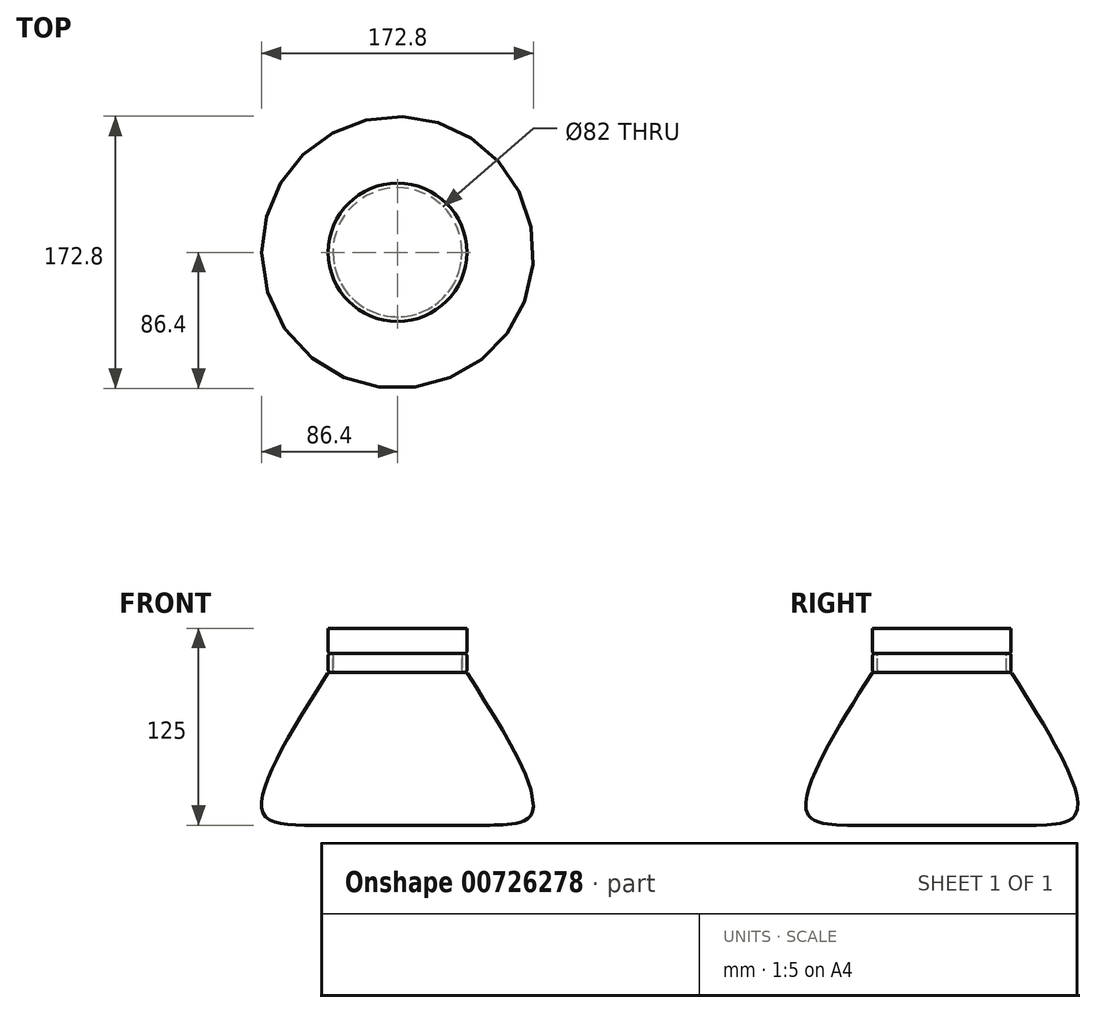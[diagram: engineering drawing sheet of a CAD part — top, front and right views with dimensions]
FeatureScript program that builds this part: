
annotation { "Feature Type Name" : "Feature", "Feature Type Description" : "" }
export const myFeature = defineFeature(function(context is Context, id is Id, definition is map)
    precondition{}
    {
        {
            var Q0;
            Q0=qCreatedBy(makeId("Front.planeOp"),FACE);
            var sketch = newSketch(context, id + "F0", { "sketchPlane" : qUnion([Q0])});
            skLineSegment(sketch, "E0", {"start": v(50, 0) * mm, "end": v(0, 0) * mm});
            skLineSegment(sketch, "E1", {"start": v(0, 0) * mm, "end": v(0, 125) * mm});
            skLineSegment(sketch, "E2", {"start": v(0, 125) * mm, "end": v(44, 125) * mm});
            skLineSegment(sketch, "E3", {"start": v(44, 125) * mm, "end": v(44, 109) * mm});
            skLineSegment(sketch, "E4", {"start": v(44, 109) * mm, "end": v(41, 109) * mm});
            skLineSegment(sketch, "E5", {"start": v(41, 109) * mm, "end": v(41, 97) * mm});
            skLineSegment(sketch, "E6", {"start": v(41, 97) * mm, "end": v(44, 97) * mm});
            skFitSpline(sketch, "E7", {"points": [v(44, 97) * mm, v(86, 9.34) * mm, v(50, 0) * mm], "startDerivative": vector(95.1, -149.17) * mm, "endDerivative": vector(-152.65, 0) * mm});
            skSolve(sketch);
        }
        {
            var Q0;
            Q0 = qSketchRegion(id + "F0", true);
            var Q1;
            Q1=sQuery(id+"F0.wireOp",EDGE,"E1");
            revolve(context, id + "F1", {"surfaceOperationType" : NewSurfaceOperationType.NEW, "entities" : qUnion([Q0]), "axis" : qUnion([Q1]), "revolveType" : RevolveType.FULL});
        }
        {
            var Q0;
            Q0=makeQuery(id+"F1.opRevolve","SWEPT_EDGE",EDGE,{"disambiguationData":[OSD([sQuery(id+"F0.wireOp",EDGE,"E3"),sQuery(id+"F0.wireOp",EDGE,"E4")])]});
            var Q1;
            Q1=makeQuery(id+"F1.opRevolve","SWEPT_EDGE",EDGE,{"disambiguationData":[OSD([sQuery(id+"F0.wireOp",EDGE,"E5"),sQuery(id+"F0.wireOp",EDGE,"E6")])]});
            var Q2;
            Q2=makeQuery(id+"F1.opRevolve","SWEPT_FACE",FACE,{"disambiguationData":[OSD([sQuery(id+"F0.wireOp",EDGE,"E7")])]});
            var Q3;
            Q3=makeQuery(id+"F1.opRevolve","SWEPT_EDGE",EDGE,{"disambiguationData":[OSD([sQuery(id+"F0.wireOp",EDGE,"E4"),sQuery(id+"F0.wireOp",EDGE,"E5")])]});
            fillet(context, id + "F2", {"entities" : qUnion([Q0, Q1, Q2, Q3]), "radius" : 1.5 * mm, "tangentPropagation" : true, "allowEdgeOverflow" : false});
        }
        {
            var Q0;
            Q0=qCreatedBy(makeId("Front.planeOp"),FACE);
            var sketch = newSketch(context, id + "F3", { "sketchPlane" : qUnion([Q0])});
            skArc(sketch, "E8", {"start": v(44, 107.5) * mm, "mid": v(42.5, 109) * mm, "end": v(41, 107.5) * mm});
            skLineSegment(sketch, "E9", {"start": v(41, 107.5) * mm, "end": v(41, 98.5) * mm});
            skArc(sketch, "E10", {"start": v(41, 98.5) * mm, "mid": v(42.5, 97) * mm, "end": v(44, 98.5) * mm});
            skLineSegment(sketch, "E11", {"start": v(44, 107.5) * mm, "end": v(44, 98.5) * mm});
            skSolve(sketch);
        }
        {
            var Q0;
            Q0 = qSketchRegion(id + "F3", true);
            var Q1;
            Q1=makeQuery(id+"F1.opRevolve","SWEPT_EDGE",EDGE,{"disambiguationData":[OSD([sQuery(id+"F0.wireOp",EDGE,"E2"),sQuery(id+"F0.wireOp",EDGE,"E3")])]});
            revolve(context, id + "F4", {"surfaceOperationType" : NewSurfaceOperationType.NEW, "entities" : qUnion([Q0]), "axis" : qUnion([Q1]), "revolveType" : RevolveType.FULL});
        }
    });
